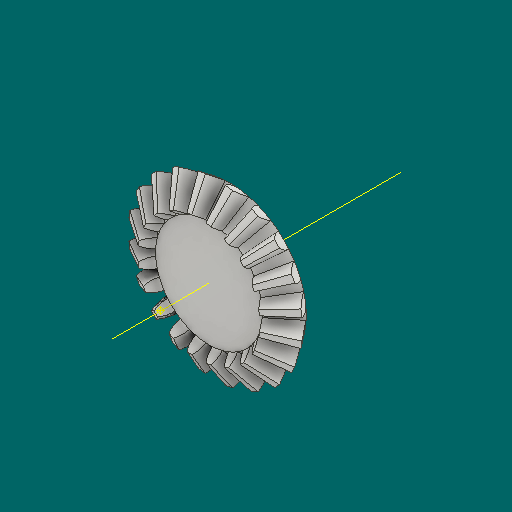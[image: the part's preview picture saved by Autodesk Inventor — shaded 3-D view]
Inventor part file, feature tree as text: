
AUTODESK INVENTOR PART (.ipt)
format: ipt  version: 2023.1 (Build 271208000, 208)  size: 467,968 bytes
history: native  units: mm
features: other x24, loft x2, pattern_circular x2, sketch x1
ambient origin geometry x6: Origin, XZ Plane, X Axis, Y Axis, Z Axis, Center Point
bodies: Solid1 (feature_tree)
feature tree (29):
  other  "Top Point"
  other  "Mesh Plane2"
  other  "Teeth Body"
  other  "Start Point"
  other  "Tooth Plane"
  other  "Start Sketch"
  other  "End Point"
  other  "3D Sketch Right"
  other  "End Plane Right"
  loft  "Loft Right"
  pattern_circular  "Circular Pattern Right"  [2 undecoded]
  other  "3D Sketch Left"
  other  "End Plane Left"
  loft  "Loft Left"
  pattern_circular  "Circular Pattern Left"  [2 undecoded]
  other  "Fix Body"
  other  "Mesh Plane"
  other  "Top Plane"
  other  "Teeth Body Sketch"
  other  "End Plane"
  other  "End Sketch"
  other  "Helical Curve Left"
  other  "End Sketch Left"
  other  "Body Sketch"
  sketch  "Sketch6"  dims[d0=25.4mm d1=23.5712mm d2=26.924mm d3=4.7625mm d4=8.509mm d5=90.0deg d7=5.878924mm d8=6.588838mm d9=19.328214mm d11=4.9022mm d12=4.063513mm d15=4.554205mm d16=13.359661mm d17=0.0mm d18=90.0deg d19=0.0mm d20=90.0deg d21=200.0mm d22=360.0deg d26=70.487871mm d27=2.94132mm d28=25.4mm d29=-9.272952mm d30=4.063513mm d31=4.554205mm d32=13.359661mm d35=0.0mm d37=0.0mm d39=0.0mm d40=90.0deg d41=200.0mm d42=360.0deg d46=90.0deg d47=90.0deg d48=0.0mm d49=0.0mm d50=90.0deg d51=1.570796mm d52=0.0mm d53=0.0mm d54=0.0mm d56=5.655365mm d57=23.274867mm d58=19.307387mm d59=16.087588mm d60=13.345266mm d61=16.087588mm d62=13.345266mm d63=90.0deg d64=90.0deg d65=70.487871mm d66=31.5mm d67=25.4mm d68=-9.272952mm d69=2.94132mm d70=4.554205mm d71=13.359661mm d72=4.063513mm d73=13.345266mm d74=16.087588mm d75=0.0mm d76=90.0deg d77=0.0mm d78=90.0deg d79=0.0mm d80=90.0deg d81=200.0mm d82=360.0deg d84=10.0mm d85=20.0mm d86=20.0mm d87=10.0mm d88=0.0mm d89=0.0mm]
  other  "Srf1"
  other  "Helical Curve Right"
  other  "End Sketch Right"
  other  "Pitch Diameter"
note: 4 required parameter values undecoded (feature->parameter linkage not recoverable at this tier; creation-order binding heuristic only, values carry confidence <= 0.55)
